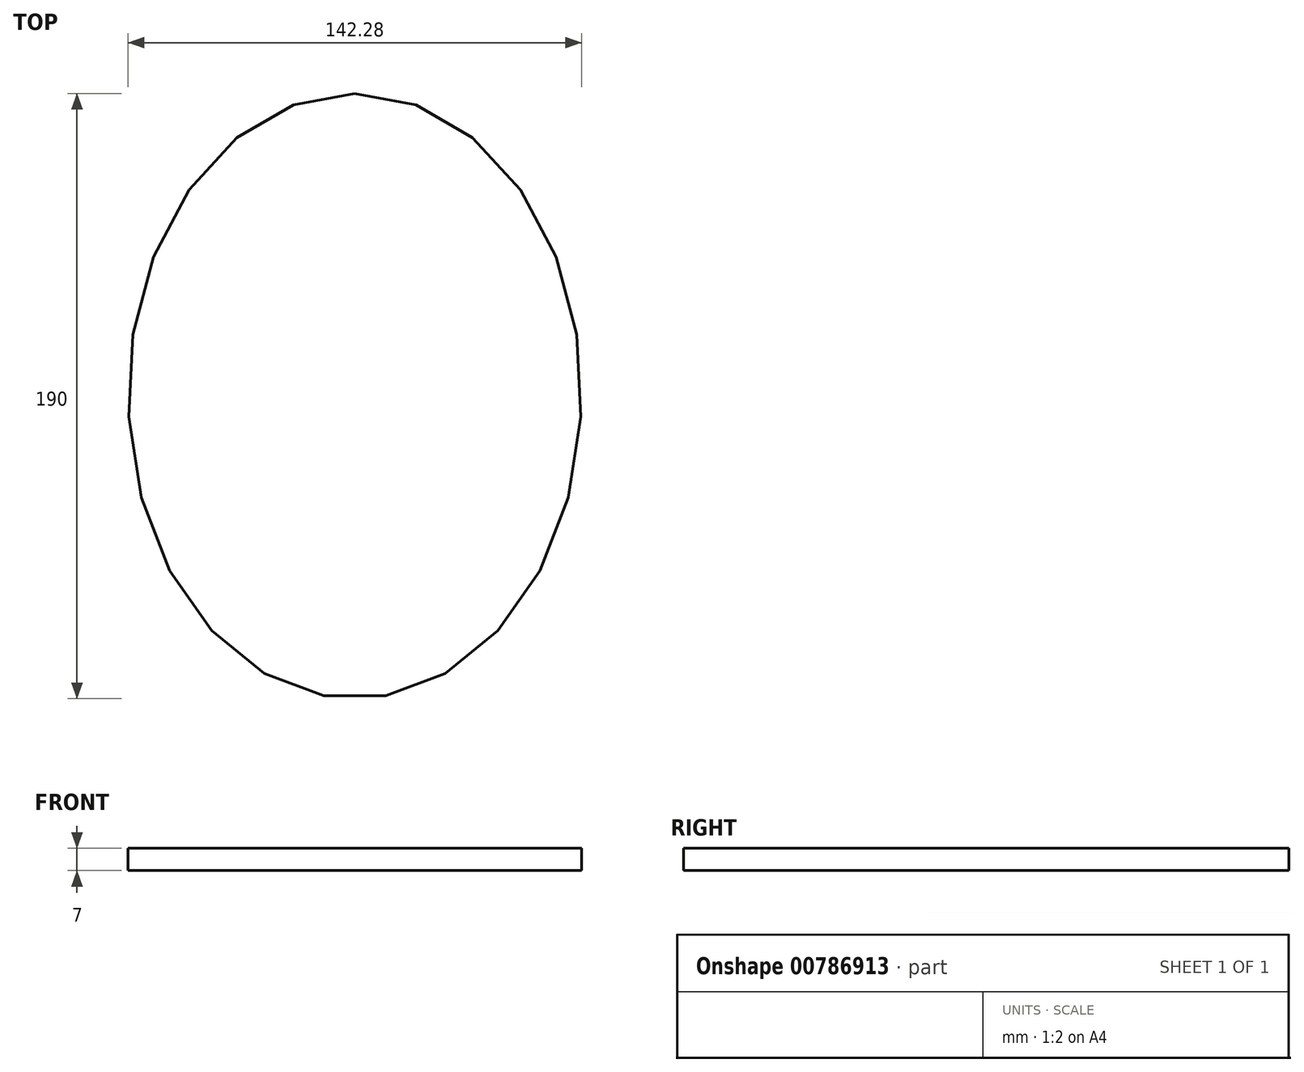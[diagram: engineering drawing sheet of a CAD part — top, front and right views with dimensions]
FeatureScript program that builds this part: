
annotation { "Feature Type Name" : "Feature", "Feature Type Description" : "" }
export const myFeature = defineFeature(function(context is Context, id is Id, definition is map)
    precondition{}
    {
        {
            var Q0;
            Q0=qCreatedBy(makeId("Top.planeOp"),FACE);
            var sketch = newSketch(context, id + "F0", { "sketchPlane" : qUnion([Q0])});
            skEllipse(sketch, "E0", {"center": v(0, 0) * mm, "majorRadius": 95 * mm, "minorRadius": 71.14 * mm, "majorAxis": v(0, 1)});
            skSolve(sketch);
        }
        {
            var Q0;
            Q0 = qSketchRegion(id + "F0", true);
            extrude(context, id + "F1", {"entities" : qUnion([Q0]), "depth" : 7 * mm, "offsetDistance" : 25 * mm});
        }
    });
